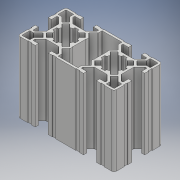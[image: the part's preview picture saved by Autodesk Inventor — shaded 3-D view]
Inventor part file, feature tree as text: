
AUTODESK INVENTOR PART (.ipt)
format: ipt  version: 2018 (Build 220112000, 112)  size: 573,952 bytes
history: native  units: mm
features: other x1, extrude x1, sketch x1
ambient origin geometry x8: Origin, YZ Plane, XZ Plane, XY Plane, X Axis, Y Axis, Z Axis, Center Point
bodies: Body1 (feature_tree)
feature tree (3):
  other  "Sólido1"
  extrude  "Extrusão1"  [1 undecoded]
  sketch  "Esboço1"  dims[d0=44.0mm d1=0.0mm]
note: 1 required parameter value undecoded (feature->parameter linkage not recoverable at this tier; creation-order binding heuristic only, values carry confidence <= 0.55)
